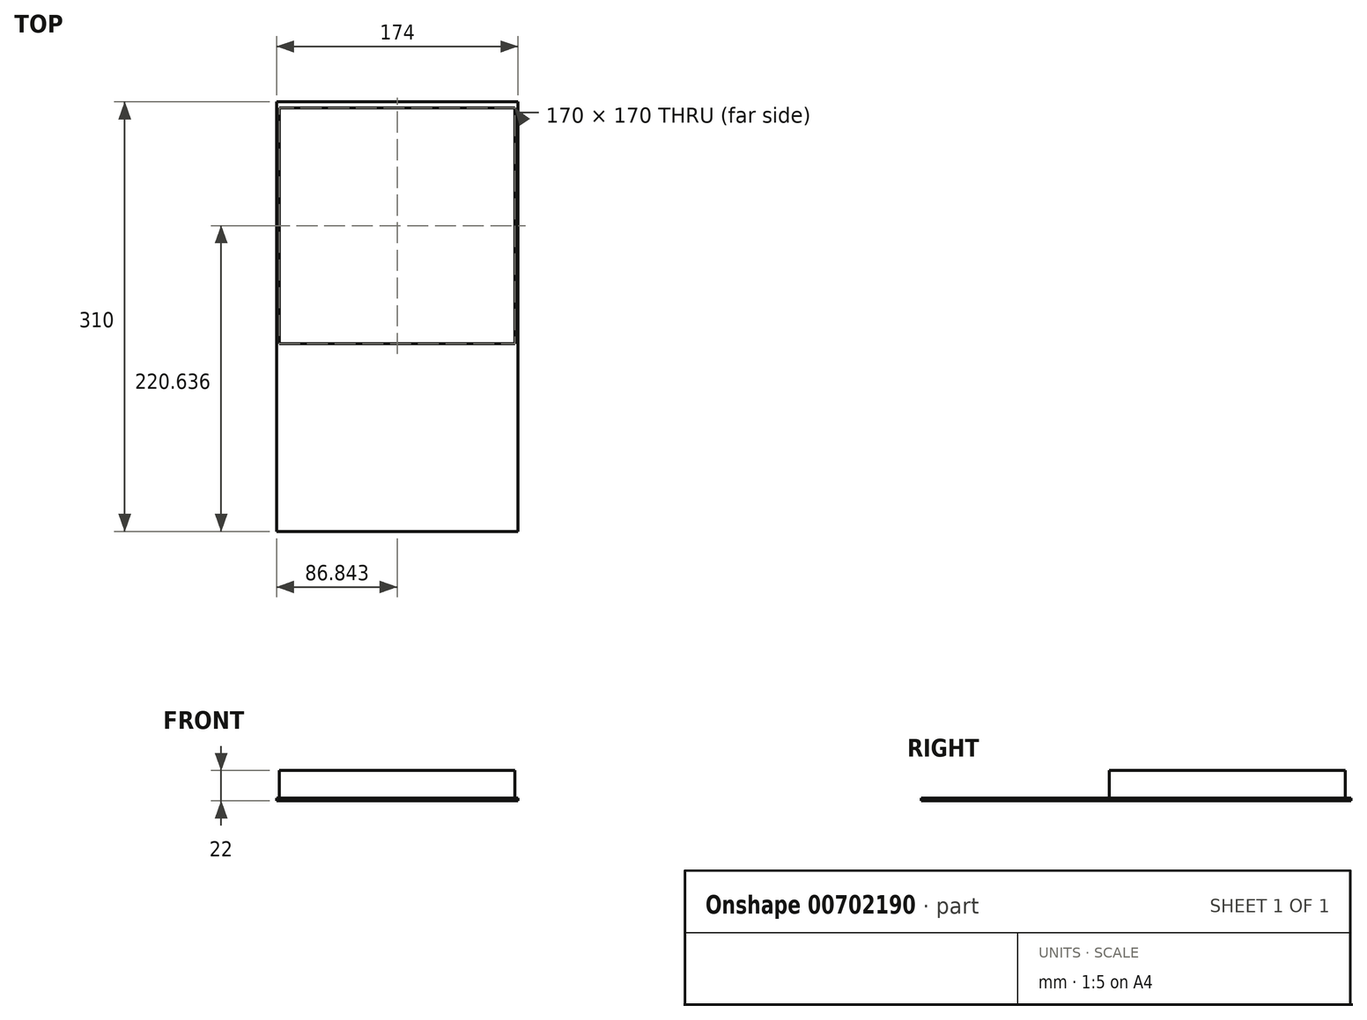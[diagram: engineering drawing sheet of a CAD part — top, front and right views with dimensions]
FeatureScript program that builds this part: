
annotation { "Feature Type Name" : "Feature", "Feature Type Description" : "" }
export const myFeature = defineFeature(function(context is Context, id is Id, definition is map)
    precondition{}
    {
        {
            var Q0;
            Q0=qCreatedBy(makeId("Top.planeOp"),FACE);
            var sketch = newSketch(context, id + "F0", { "sketchPlane" : qUnion([Q0])});
            skLineSegment(sketch, "E0.bottom", {"start": v(-59.5, 49.79) * mm, "end": v(110.5, 49.79) * mm});
            skLineSegment(sketch, "E0.top", {"start": v(-59.5, -120.21) * mm, "end": v(110.5, -120.21) * mm});
            skLineSegment(sketch, "E0.left", {"start": v(-59.5, 49.79) * mm, "end": v(-59.5, -120.21) * mm});
            skLineSegment(sketch, "E0.right", {"start": v(110.5, 49.79) * mm, "end": v(110.5, -120.21) * mm});
            skSolve(sketch);
        }
        {
            var Q0;
            Q0=makeQuery(id+"F0.imprint","IMPRINT",FACE,{"disambiguationData":[TD([[makeQuery(id+"F0.imprint","IMPRINT",EDGE,{"derivedFrom":sQuery(id+"F0.wireOp",EDGE,"E0.bottom")}),-1.0]])]});
            var sketch = newSketch(context, id + "F1", { "sketchPlane" : qUnion([Q0])});
            skSolve(sketch);
        }
        {
            var Q0;
            Q0 = qSketchRegion(id + "F0", true);
            extrude(context, id + "F2", {"entities" : qUnion([Q0]), "depth" : 20 * mm, "offsetDistance" : 25 * mm});
        }
        {
            var Q0;
            Q0=makeQuery(id+"F1.imprint","IMPRINT",FACE,{"disambiguationData":[TD([[makeQuery(id+"F1.imprint","IMPRINT",EDGE,{"derivedFrom":makeQuery(id+"F0.imprint","IMPRINT",EDGE,{"derivedFrom":sQuery(id+"F0.wireOp",EDGE,"E0.bottom")})}),-1.0]])]});
            var sketch = newSketch(context, id + "F3", { "sketchPlane" : qUnion([Q0])});
            skLineSegment(sketch, "E1.bottom", {"start": v(-61.35, 54.15) * mm, "end": v(112.65, 54.15) * mm});
            skLineSegment(sketch, "E1.top", {"start": v(-61.35, -255.85) * mm, "end": v(112.65, -255.85) * mm});
            skLineSegment(sketch, "E1.left", {"start": v(-61.35, 54.15) * mm, "end": v(-61.35, -255.85) * mm});
            skLineSegment(sketch, "E1.right", {"start": v(112.65, 54.15) * mm, "end": v(112.65, -255.85) * mm});
            skSolve(sketch);
        }
        {
            var Q0;
            Q0=makeQuery(id+"F3.imprint","IMPRINT",FACE,{"disambiguationData":[TD([[makeQuery(id+"F3.imprint","IMPRINT",EDGE,{"derivedFrom":sQuery(id+"F3.wireOp",EDGE,"E1.bottom")}),-1.0]])]});
            var Q1;
            Q1=makeQuery(id+"F2.opExtrude","CAP_FACE",FACE,{"disambiguationData":[OSD([sQuery(id+"F0.wireOp",EDGE,"E0.bottom"),sQuery(id+"F0.wireOp",EDGE,"E0.top"),sQuery(id+"F0.wireOp",EDGE,"E0.left"),sQuery(id+"F0.wireOp",EDGE,"E0.right")])],"isStart":false});
            extrude(context, id + "F4", {"entities" : qUnion([Q0, Q1]), "operationType" : NewBodyOperationType.ADD, "oppositeDirection" : true, "depth" : 2 * mm, "offsetDistance" : 25 * mm});
        }
    });
